# Revit family: TTUFS4.5X30
name_source: partatom
category: Structural Connections
revit_build: Autodesk Revit 2014 (Build: 20130308_1515(x64)
units: mm (PartAtom-declared; Revit-internal decimal feet)

## types (1)
- TTUFS4.5X30
    Default Elevation = 0 mm  [stored 0 ft]
    Density = 0.00217 kg
    Description = Screws
    EPD = https://www.strongtie.eu
    ETA / DoP = https://www.strongtie.eu
    Manufacturer = Simpson Strong-Tie
    Model = TTUFS4.5x30
    Model Disclaimer = Contact Simpson Strong-Tie Company  for more information
    Name = TTUFS4.5x30
    ObjectType = TTUFS4.5x30
    Product Material = ElectroGalvanised
    Product Type = Screws
    Reference = 74435
    Technical datasheet = https://www.strongtie.eu
    URL = www.strongtie.eu
    UniClass Number = Pr_20_29_76_98
    UniClass Title = Wood screws

note: [stored X ft] marks values corroborated as IEEE doubles in the binary element streams (Revit-internal decimal feet)

## geometry (parser evidence)
native form markers: Blend x33, Sweep x1
no freeform markers — native parametric forms only
